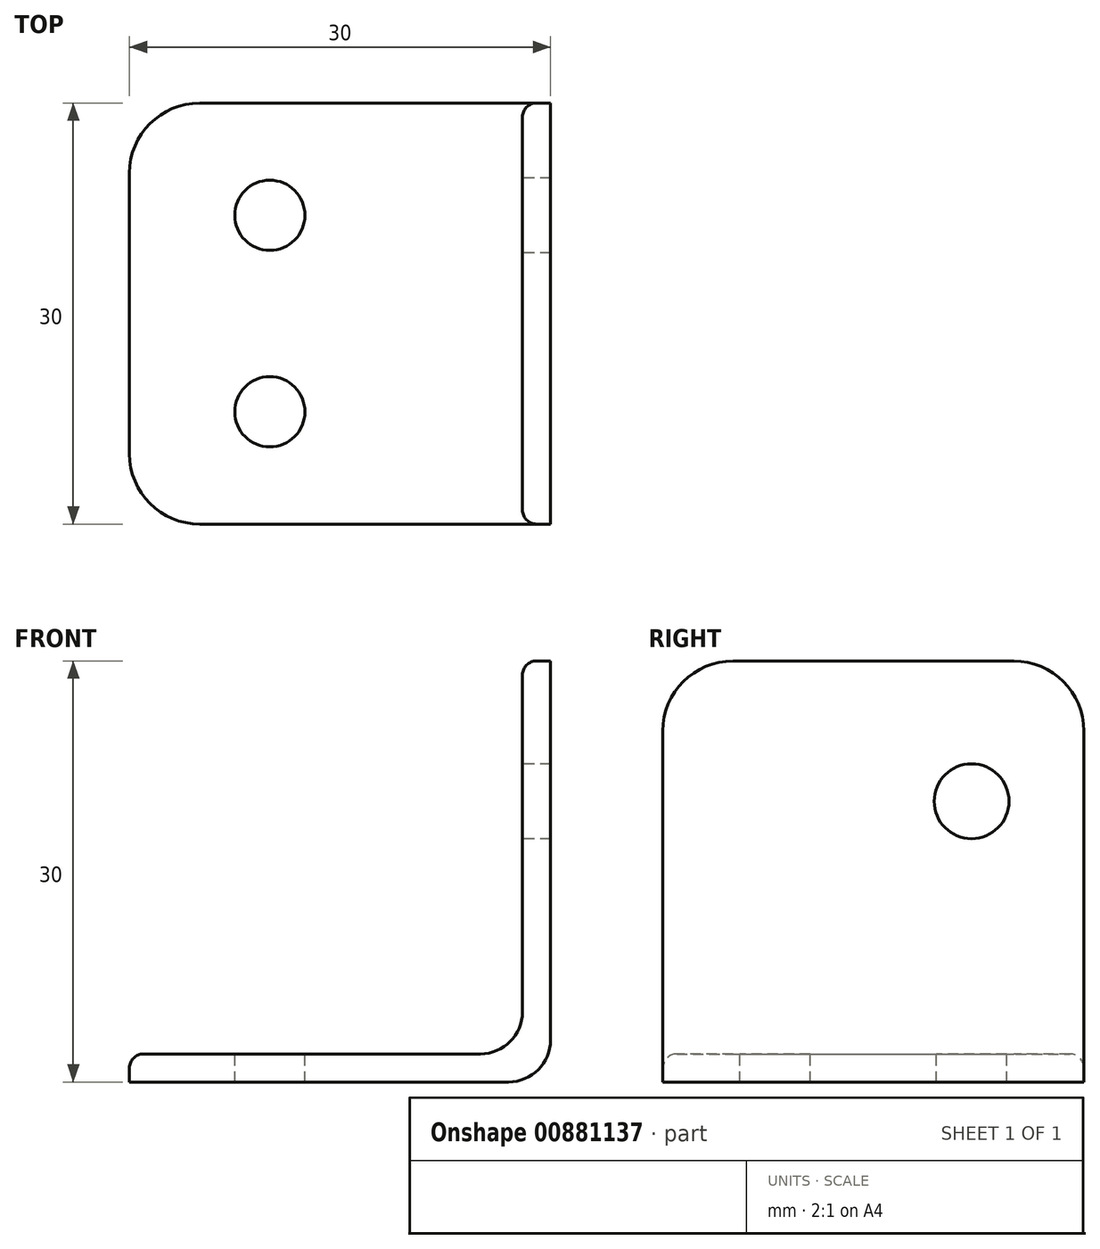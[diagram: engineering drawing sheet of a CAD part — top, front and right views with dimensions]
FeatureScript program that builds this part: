
annotation { "Feature Type Name" : "Feature", "Feature Type Description" : "" }
export const myFeature = defineFeature(function(context is Context, id is Id, definition is map)
    precondition{}
    {
        {
            var Q0;
            Q0=qCreatedBy(makeId("Front.planeOp"),FACE);
            var sketch = newSketch(context, id + "F0", { "sketchPlane" : qUnion([Q0])});
            skLineSegment(sketch, "E0", {"start": v(-30, 0) * mm, "end": v(0, 0) * mm});
            skLineSegment(sketch, "E1", {"start": v(0, 0) * mm, "end": v(0, 30) * mm});
            skLineSegment(sketch, "E2", {"start": v(-30, 0) * mm, "end": v(-30, 2) * mm});
            skLineSegment(sketch, "E3", {"start": v(-30, 2) * mm, "end": v(-2, 2) * mm});
            skLineSegment(sketch, "E4", {"start": v(-2, 2) * mm, "end": v(-2, 30) * mm});
            skLineSegment(sketch, "E5", {"start": v(-2, 30) * mm, "end": v(0, 30) * mm});
            skSolve(sketch);
        }
        {
            var Q0;
            Q0=makeQuery(id+"F0.imprint","IMPRINT",FACE,{"disambiguationData":[TD([[makeQuery(id+"F0.imprint","IMPRINT",EDGE,{"derivedFrom":sQuery(id+"F0.wireOp",EDGE,"E0")}),1.0]])]});
            extrude(context, id + "F1", {"entities" : qUnion([Q0]), "endBound" : BoundingType.SYMMETRIC, "depth" : 30 * mm, "offsetDistance" : 25 * mm});
        }
        {
            var Q0;
            Q0=makeQuery(id+"F1.opExtrude","SWEPT_EDGE",EDGE,{"disambiguationData":[OSD([sQuery(id+"F0.wireOp",EDGE,"E0"),sQuery(id+"F0.wireOp",EDGE,"E1")])]});
            var Q1;
            Q1=makeQuery(id+"F1.opExtrude","SWEPT_EDGE",EDGE,{"disambiguationData":[OSD([sQuery(id+"F0.wireOp",EDGE,"E3"),sQuery(id+"F0.wireOp",EDGE,"E4")])]});
            fillet(context, id + "F2", {"entities" : qUnion([Q0, Q1]), "radius" : 3 * mm, "tangentPropagation" : true, "allowEdgeOverflow" : false});
        }
        {
            var Q0;
            Q0=makeQuery(id+"F1.opExtrude","SWEPT_FACE",FACE,{"disambiguationData":[OSD([sQuery(id+"F0.wireOp",EDGE,"E3")])]});
            var sketch = newSketch(context, id + "F3", { "sketchPlane" : qUnion([Q0])});
            skCircle(sketch, "E6", {"center": v(-20, 7) * mm, "radius": 2.5 * mm});
            skCircle(sketch, "E7", {"center": v(-20, -7) * mm, "radius": 2.5 * mm});
            skSolve(sketch);
        }
        {
            var Q0;
            Q0=makeQuery(id+"F3.imprint","IMPRINT",FACE,{"disambiguationData":[TD([[makeQuery(id+"F3.imprint","IMPRINT",EDGE,{"derivedFrom":sQuery(id+"F3.wireOp",EDGE,"E6")}),1.0]])]});
            var Q1;
            Q1=makeQuery(id+"F3.imprint","IMPRINT",FACE,{"disambiguationData":[TD([[makeQuery(id+"F3.imprint","IMPRINT",EDGE,{"derivedFrom":sQuery(id+"F3.wireOp",EDGE,"E7")}),1.0]])]});
            extrude(context, id + "F4", {"entities" : qUnion([Q0, Q1]), "operationType" : NewBodyOperationType.REMOVE, "endBound" : BoundingType.THROUGH_ALL, "oppositeDirection" : true, "depth" : 25 * mm, "offsetDistance" : 25 * mm});
        }
        {
            var Q0;
            Q0=makeQuery(id+"F1.opExtrude","CAP_EDGE",EDGE,{"disambiguationData":[OSD([sQuery(id+"F0.wireOp",EDGE,"E2")])],"isStart":false});
            var Q1;
            Q1=makeQuery(id+"F1.opExtrude","CAP_EDGE",EDGE,{"disambiguationData":[OSD([sQuery(id+"F0.wireOp",EDGE,"E2")])],"isStart":true});
            var Q2;
            Q2=makeQuery(id+"F1.opExtrude","CAP_EDGE",EDGE,{"disambiguationData":[OSD([sQuery(id+"F0.wireOp",EDGE,"E5")])],"isStart":false});
            var Q3;
            Q3=makeQuery(id+"F1.opExtrude","CAP_EDGE",EDGE,{"disambiguationData":[OSD([sQuery(id+"F0.wireOp",EDGE,"E5")])],"isStart":true});
            fillet(context, id + "F5", {"entities" : qUnion([Q0, Q1, Q2, Q3]), "radius" : 5 * mm, "tangentPropagation" : true, "allowEdgeOverflow" : false});
        }
        {
            var Q0;
            Q0=makeQuery(id+"F1.opExtrude","CAP_EDGE",EDGE,{"disambiguationData":[OSD([sQuery(id+"F0.wireOp",EDGE,"E3")])],"isStart":true});
            fillet(context, id + "F6", {"entities" : qUnion([Q0]), "radius" : 1 * mm, "tangentPropagation" : true, "allowEdgeOverflow" : false});
        }
        {
            var Q0;
            Q0=makeQuery(id+"F1.opExtrude","SWEPT_FACE",FACE,{"disambiguationData":[OSD([sQuery(id+"F0.wireOp",EDGE,"E4")])]});
            var sketch = newSketch(context, id + "F7", { "sketchPlane" : qUnion([Q0])});
            skCircle(sketch, "E8", {"center": v(-7, 20) * mm, "radius": 2.67 * mm});
            skSolve(sketch);
        }
        {
            var Q0;
            Q0=makeQuery(id+"F7.imprint","IMPRINT",FACE,{"disambiguationData":[TD([[makeQuery(id+"F7.imprint","IMPRINT",EDGE,{"derivedFrom":sQuery(id+"F7.wireOp",EDGE,"E8")}),1.0]])]});
            extrude(context, id + "F8", {"entities" : qUnion([Q0]), "operationType" : NewBodyOperationType.REMOVE, "endBound" : BoundingType.THROUGH_ALL, "oppositeDirection" : true, "depth" : 25 * mm, "offsetDistance" : 25 * mm});
        }
    });
